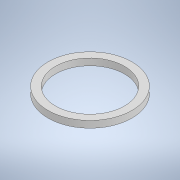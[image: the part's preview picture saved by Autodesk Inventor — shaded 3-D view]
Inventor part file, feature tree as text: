
AUTODESK INVENTOR PART (.ipt)
format: ipt  version: 2021 (Build 250183000, 183)  size: 99,840 bytes
history: native  units: mm
features: extrude x1, sketch x1
ambient origin geometry x8: Origin, YZ Plane, XZ Plane, XY Plane, X Axis, Y Axis, Z Axis, Center Point
bodies: Solid1 (feature_tree)
feature tree (2):
  extrude  "Extrusion1"  Depth=10.0mm
  sketch  "Sketch1"  dims[d0=8.2mm d1=10.0mm d2=0.8mm d3=0.0mm]
